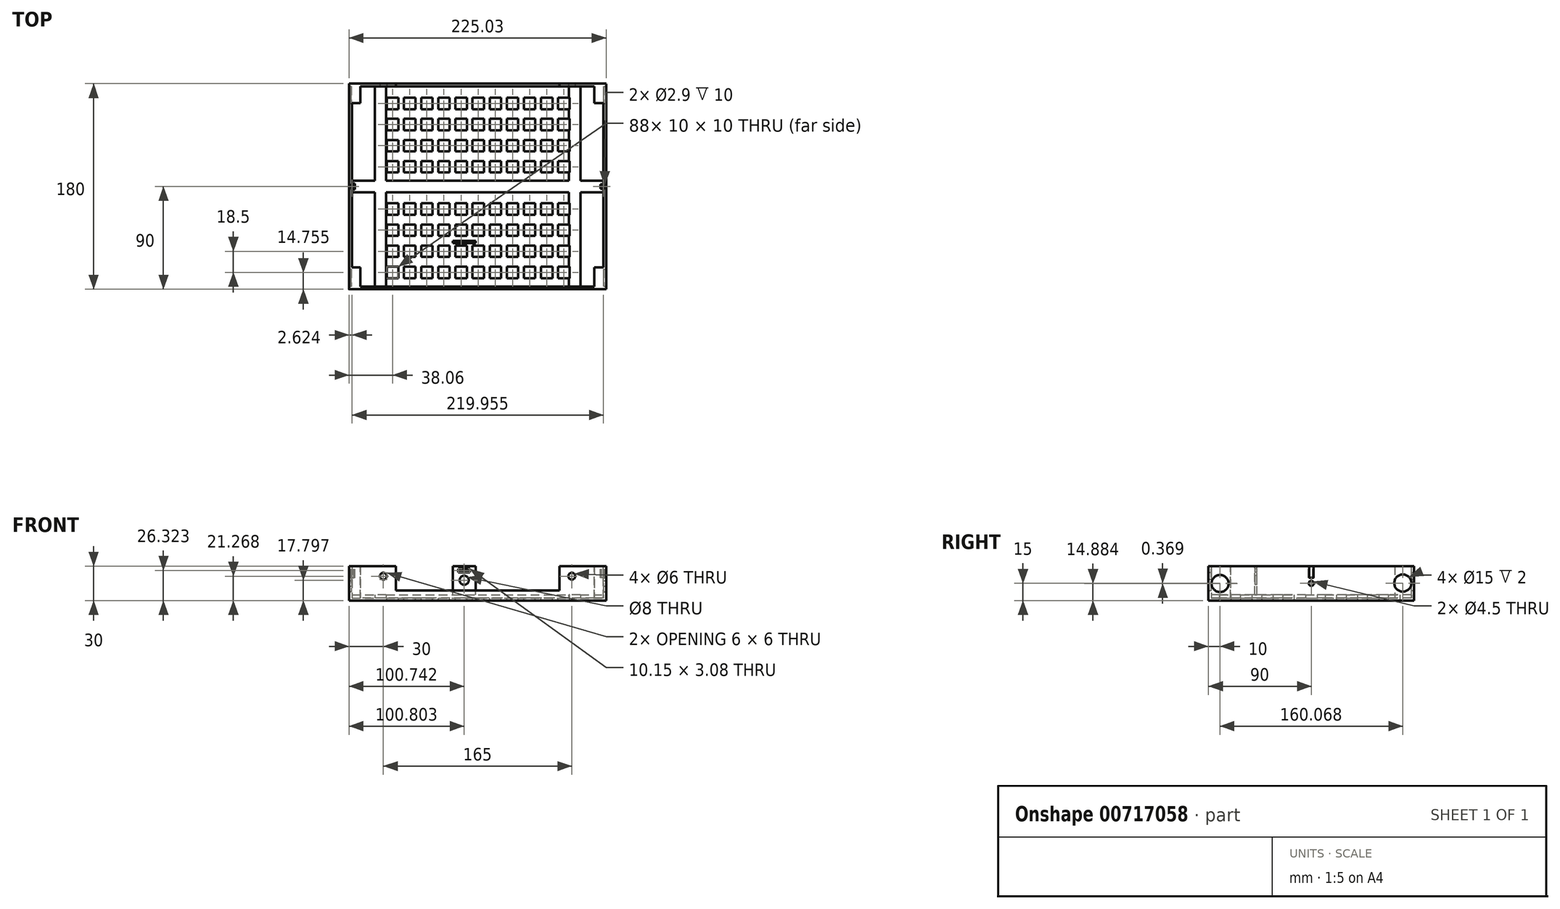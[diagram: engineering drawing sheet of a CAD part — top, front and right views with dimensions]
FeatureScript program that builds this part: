
annotation { "Feature Type Name" : "Feature", "Feature Type Description" : "" }
export const myFeature = defineFeature(function(context is Context, id is Id, definition is map)
    precondition{}
    {
        {
            var Q0;
            Q0=qCreatedBy(makeId("Top.planeOp"),FACE);
            var sketch = newSketch(context, id + "F0", { "sketchPlane" : qUnion([Q0])});
            skLineSegment(sketch, "E0.bottom", {"start": v(112.5, -90) * mm, "end": v(-112.5, -90) * mm});
            skLineSegment(sketch, "E0.top", {"start": v(112.5, 90) * mm, "end": v(-112.5, 90) * mm});
            skLineSegment(sketch, "E0.left", {"start": v(112.5, -90) * mm, "end": v(112.5, 90) * mm});
            skLineSegment(sketch, "E0.right", {"start": v(-112.5, -90) * mm, "end": v(-112.5, 90) * mm});
            skPoint(sketch, "E0.middle", {"position": v(0, 0) * mm});
            skSolve(sketch);
        }
        {
            var Q0;
            Q0=makeQuery(id+"F0.imprint","IMPRINT",FACE,{"disambiguationData":[TD([[makeQuery(id+"F0.imprint","IMPRINT",EDGE,{"derivedFrom":sQuery(id+"F0.wireOp",EDGE,"E0.bottom")}),-1.0]])]});
            extrude(context, id + "F1", {"entities" : qUnion([Q0]), "depth" : 30 * mm, "offsetDistance" : 25 * mm});
        }
        {
            var Q0;
            Q0=makeQuery(id+"F1.opExtrude","CAP_FACE",FACE,{"disambiguationData":[OSD([sQuery(id+"F0.wireOp",EDGE,"E0.bottom"),sQuery(id+"F0.wireOp",EDGE,"E0.top"),sQuery(id+"F0.wireOp",EDGE,"E0.left"),sQuery(id+"F0.wireOp",EDGE,"E0.right")])],"isStart":false});
            var sketch = newSketch(context, id + "F2", { "sketchPlane" : qUnion([Q0])});
            skLineSegment(sketch, "E1.bottom", {"start": v(110, -87.5) * mm, "end": v(-110, -87.5) * mm});
            skLineSegment(sketch, "E1.top", {"start": v(110, 87.5) * mm, "end": v(-110, 87.5) * mm});
            skLineSegment(sketch, "E1.left", {"start": v(110, -87.5) * mm, "end": v(110, 87.5) * mm});
            skLineSegment(sketch, "E1.right", {"start": v(-110, -87.5) * mm, "end": v(-110, 87.5) * mm});
            skPoint(sketch, "E1.middle", {"position": v(0, 0) * mm});
            skSolve(sketch);
        }
        {
            var Q0;
            Q0=makeQuery(id+"F2.imprint","IMPRINT",FACE,{"disambiguationData":[TD([[makeQuery(id+"F2.imprint","IMPRINT",EDGE,{"derivedFrom":sQuery(id+"F2.wireOp",EDGE,"E1.bottom")}),-1.0]])]});
            extrude(context, id + "F3", {"entities" : qUnion([Q0]), "operationType" : NewBodyOperationType.REMOVE, "oppositeDirection" : true, "depth" : 28 * mm, "offsetDistance" : 25 * mm});
        }
        {
            var Q0;
            Q0=makeQuery(id+"F1.opExtrude","SWEPT_FACE",FACE,{"disambiguationData":[OSD([sQuery(id+"F0.wireOp",EDGE,"E0.bottom")])]});
            var sketch = newSketch(context, id + "F4", { "sketchPlane" : qUnion([Q0])});
            skLineSegment(sketch, "E2", {"start": v(0, 15) * mm, "end": v(0, 30) * mm, "construction": true});
            skPoint(sketch, "E2.startSnap0", {"position": v(-112.5, 15) * mm});
            skPoint(sketch, "E2.startSnap1", {"position": v(0, 30) * mm});
            skLineSegment(sketch, "E3", {"start": v(0, 15) * mm, "end": v(-112.5, 15) * mm, "construction": true});
            skLineSegment(sketch, "E4", {"start": v(0, 15) * mm, "end": v(112.5, 15) * mm, "construction": true});
            skLineSegment(sketch, "E5", {"start": v(-112.5, 0) * mm, "end": v(-82.5, 0) * mm, "construction": true});
            skLineSegment(sketch, "E6", {"start": v(112.5, 0) * mm, "end": v(82.5, 0) * mm, "construction": true});
            skLineSegment(sketch, "E7", {"start": v(-82.5, 0) * mm, "end": v(-82.5, 30) * mm, "construction": true});
            skLineSegment(sketch, "E8", {"start": v(82.5, 0) * mm, "end": v(82.5, 30) * mm, "construction": true});
            skLineSegment(sketch, "E9", {"start": v(-112.5, 30) * mm, "end": v(-72.5, 30) * mm, "construction": true});
            skLineSegment(sketch, "E10", {"start": v(112.5, 30) * mm, "end": v(72.5, 30) * mm, "construction": true});
            skLineSegment(sketch, "E11", {"start": v(-112.5, 0) * mm, "end": v(-112.5, 10) * mm, "construction": true});
            skLineSegment(sketch, "E12", {"start": v(-112.5, 10) * mm, "end": v(112.5, 10) * mm, "construction": true});
            skLineSegment(sketch, "E13", {"start": v(-22.5, 30) * mm, "end": v(-22.5, 0) * mm, "construction": true});
            skLineSegment(sketch, "E14", {"start": v(22.5, 30) * mm, "end": v(22.5, 0) * mm, "construction": true});
            skFitSpline(sketch, "E15", {"points": [v(-72.5, 30) * mm, v(-71.2, 15) * mm, v(-22.5, 10) * mm], "startDerivative": vector(-3.64, -53.35) * mm, "endDerivative": vector(76.18, -37.14) * mm});
            skFitSpline(sketch, "E16", {"points": [v(72.5, 30) * mm, v(72.49, 15) * mm, v(22.5, 10) * mm], "startDerivative": vector(-2.42, -56.98) * mm, "endDerivative": vector(-66.73, -35.72) * mm});
            skLineSegment(sketch, "E17", {"start": v(-22.5, 10) * mm, "end": v(-22.5, 0) * mm});
            skLineSegment(sketch, "E18", {"start": v(22.5, 10) * mm, "end": v(22.5, 0) * mm});
            skLineSegment(sketch, "E19", {"start": v(-22.5, 10) * mm, "end": v(22.5, 10) * mm});
            skLineSegment(sketch, "E20", {"start": v(112.5, 21.27) * mm, "end": v(-112.5, 21.27) * mm, "construction": true});
            skCircle(sketch, "E21", {"center": v(82.5, 21.27) * mm, "radius": 3 * mm});
            skCircle(sketch, "E22", {"center": v(-82.5, 21.27) * mm, "radius": 3 * mm});
            skSolve(sketch);
        }
        {
            var Q0;
            Q0 = qSketchRegion(id + "F4", true);
            extrude(context, id + "F5", {"entities" : qUnion([Q0]), "operationType" : NewBodyOperationType.REMOVE, "oppositeDirection" : true, "depth" : 2500 * mm, "offsetDistance" : 25 * mm});
        }
        {
            var Q0;
            Q0=makeQuery(id+"F3.boolean.opBoolean","COPY",FACE,{"derivedFrom":makeQuery(id+"F3.opExtrude","CAP_FACE",FACE,{"disambiguationData":[OSD([sQuery(id+"F2.wireOp",EDGE,"E1.bottom"),sQuery(id+"F2.wireOp",EDGE,"E1.top"),sQuery(id+"F2.wireOp",EDGE,"E1.left"),sQuery(id+"F2.wireOp",EDGE,"E1.right")])],"isStart":false})});
            var sketch = newSketch(context, id + "F6", { "sketchPlane" : qUnion([Q0])});
            skLineSegment(sketch, "E23", {"start": v(-110, 87.5) * mm, "end": v(-90, 87.5) * mm, "construction": true});
            skLineSegment(sketch, "E24.bottom", {"start": v(-90, 87.5) * mm, "end": v(-80, 87.5) * mm});
            skLineSegment(sketch, "E24.top", {"start": v(-90, -87.5) * mm, "end": v(-80, -87.5) * mm});
            skLineSegment(sketch, "E24.left", {"start": v(-90, 87.5) * mm, "end": v(-90, -87.5) * mm});
            skLineSegment(sketch, "E24.right", {"start": v(-80, 87.5) * mm, "end": v(-80, -87.5) * mm});
            skLineSegment(sketch, "E25", {"start": v(110, 87.5) * mm, "end": v(90, 87.5) * mm, "construction": true});
            skLineSegment(sketch, "E26.bottom", {"start": v(90, 87.5) * mm, "end": v(80, 87.5) * mm});
            skLineSegment(sketch, "E26.top", {"start": v(90, -87.5) * mm, "end": v(80, -87.5) * mm});
            skLineSegment(sketch, "E26.left", {"start": v(90, 87.5) * mm, "end": v(90, -87.5) * mm});
            skLineSegment(sketch, "E26.right", {"start": v(80, 87.5) * mm, "end": v(80, -87.5) * mm});
            skLineSegment(sketch, "E27.bottom", {"start": v(-110, 5) * mm, "end": v(110, 5) * mm});
            skLineSegment(sketch, "E27.top", {"start": v(-110, -5) * mm, "end": v(110, -5) * mm});
            skLineSegment(sketch, "E27.left", {"start": v(-110, 5) * mm, "end": v(-110, -5) * mm});
            skLineSegment(sketch, "E27.right", {"start": v(110, 5) * mm, "end": v(110, -5) * mm});
            skPoint(sketch, "E27.middle", {"position": v(0, 0) * mm});
            skSolve(sketch);
        }
        {
            var Q0;
            Q0=makeQuery(id+"F6.imprint","IMPRINT",FACE,{"disambiguationData":[TD([[makeQuery(id+"F6.imprint","IMPRINT",EDGE,{"derivedFrom":sQuery(id+"F6.wireOp",EDGE,"E24.bottom")}),1.0]])]});
            var Q1;
            Q1=makeQuery(id+"F6.imprint","IMPRINT",FACE,{"disambiguationData":[TD([[makeQuery(id+"F6.imprint","IMPRINT",EDGE,{"derivedFrom":sQuery(id+"F6.wireOp",EDGE,"E26.bottom")}),1.0]])]});
            var Q2;
            {var subQ5=sQuery(id+"F6.wireOp",EDGE,"E27.left");Q2=makeQuery(id+"F6.imprint","IMPRINT",FACE,{"disambiguationData":[TD([[makeQuery(id+"F6.imprint","IMPRINT",EDGE,{"derivedFrom":subQ5}),-1.0]])]});}
            var Q3;
            {var subQ0=sQuery(id+"F6.wireOp",EDGE,"E27.bottom");var subQ1=sQuery(id+"F6.wireOp",EDGE,"E24.left");var subQ2=makeQuery(id+"F6.imprint","INTERSECT",VERTEX,{"derivedFrom":[subQ1,subQ0]});Q3=makeQuery(id+"F6.imprint","IMPRINT",FACE,{"disambiguationData":[TD([[makeQuery(id+"F6.imprint","IMPRINT",EDGE,{"disambiguationData":[TD([[subQ2,-1.0]])],"derivedFrom":subQ1}),1.0]])]});}
            var Q4;
            {var subQ0=sQuery(id+"F6.wireOp",EDGE,"E24.top");Q4=makeQuery(id+"F6.imprint","IMPRINT",FACE,{"disambiguationData":[TD([[makeQuery(id+"F6.imprint","IMPRINT",EDGE,{"derivedFrom":subQ0}),-1.0]])]});}
            var Q5;
            {var subQ0=sQuery(id+"F6.wireOp",EDGE,"E27.bottom");var subQ1=sQuery(id+"F6.wireOp",EDGE,"E24.right");var subQ2=makeQuery(id+"F6.imprint","INTERSECT",VERTEX,{"derivedFrom":[subQ1,subQ0]});Q5=makeQuery(id+"F6.imprint","IMPRINT",FACE,{"disambiguationData":[TD([[makeQuery(id+"F6.imprint","IMPRINT",EDGE,{"disambiguationData":[TD([[subQ2,-1.0]])],"derivedFrom":subQ1}),1.0]])]});}
            var Q6;
            {var subQ0=sQuery(id+"F6.wireOp",EDGE,"E27.bottom");var subQ1=sQuery(id+"F6.wireOp",EDGE,"E26.left");var subQ2=makeQuery(id+"F6.imprint","INTERSECT",VERTEX,{"derivedFrom":[subQ1,subQ0]});Q6=makeQuery(id+"F6.imprint","IMPRINT",FACE,{"disambiguationData":[TD([[makeQuery(id+"F6.imprint","IMPRINT",EDGE,{"disambiguationData":[TD([[subQ2,-1.0]])],"derivedFrom":subQ1}),-1.0]])]});}
            var Q7;
            {var subQ0=sQuery(id+"F6.wireOp",EDGE,"E26.top");Q7=makeQuery(id+"F6.imprint","IMPRINT",FACE,{"disambiguationData":[TD([[makeQuery(id+"F6.imprint","IMPRINT",EDGE,{"derivedFrom":subQ0}),-1.0]])]});}
            var Q8;
            {var subQ5=sQuery(id+"F6.wireOp",EDGE,"E27.right");Q8=makeQuery(id+"F6.imprint","IMPRINT",FACE,{"disambiguationData":[TD([[makeQuery(id+"F6.imprint","IMPRINT",EDGE,{"derivedFrom":subQ5}),1.0]])]});}
            extrude(context, id + "F7", {"entities" : qUnion([Q0, Q1, Q2, Q3, Q4, Q5, Q6, Q7, Q8]), "depth" : 3 * mm, "offsetDistance" : 25 * mm});
        }
        {
            var Q0;
            Q0=makeQuery(id+"F1.opExtrude","SWEPT_FACE",FACE,{"disambiguationData":[OSD([sQuery(id+"F0.wireOp",EDGE,"E0.left")])]});
            var sketch = newSketch(context, id + "F8", { "sketchPlane" : qUnion([Q0])});
            skLineSegment(sketch, "E28", {"start": v(0, 30) * mm, "end": v(0, 0) * mm, "construction": true});
            skLineSegment(sketch, "E29", {"start": v(-90, 15) * mm, "end": v(90, 15) * mm, "construction": true});
            skCircle(sketch, "E30", {"center": v(0, 15) * mm, "radius": 2.25 * mm});
            skSolve(sketch);
        }
        {
            var Q0;
            Q0=makeQuery(id+"F8.imprint","IMPRINT",FACE,{"disambiguationData":[TD([[makeQuery(id+"F8.imprint","IMPRINT",EDGE,{"derivedFrom":sQuery(id+"F8.wireOp",EDGE,"E30")}),1.0]])]});
            extrude(context, id + "F9", {"entities" : qUnion([Q0]), "operationType" : NewBodyOperationType.REMOVE, "endBound" : BoundingType.THROUGH_ALL, "oppositeDirection" : true, "depth" : 25 * mm, "offsetDistance" : 25 * mm});
        }
        {
            var Q0;
            Q0=makeQuery(id+"F1.opExtrude","SWEPT_FACE",FACE,{"disambiguationData":[OSD([sQuery(id+"F0.wireOp",EDGE,"E0.top")])]});
            var sketch = newSketch(context, id + "F10", { "sketchPlane" : qUnion([Q0])});
            skLineSegment(sketch, "E31.bottom", {"start": v(71.59, 8.69) * mm, "end": v(-71.59, 8.69) * mm});
            skLineSegment(sketch, "E31.top", {"start": v(71.59, 51.31) * mm, "end": v(-71.59, 51.31) * mm});
            skLineSegment(sketch, "E31.left", {"start": v(71.59, 8.69) * mm, "end": v(71.59, 51.31) * mm});
            skLineSegment(sketch, "E31.right", {"start": v(-71.59, 8.69) * mm, "end": v(-71.59, 51.31) * mm});
            skPoint(sketch, "E31.middle", {"position": v(0, 30) * mm});
            skSolve(sketch);
        }
        {
            var Q0;
            {var subQ0=sQuery(id+"F10.wireOp",EDGE,"E31.bottom");Q0=makeQuery(id+"F10.imprint","IMPRINT",FACE,{"disambiguationData":[TD([[makeQuery(id+"F10.imprint","IMPRINT",EDGE,{"derivedFrom":subQ0}),-1.0]])]});}
            extrude(context, id + "F11", {"entities" : qUnion([Q0]), "operationType" : NewBodyOperationType.REMOVE, "oppositeDirection" : true, "depth" : 3000 * mm, "offsetDistance" : 25 * mm});
        }
        {
            var Q0;
            Q0=makeQuery(id+"F2.imprint","IMPRINT",FACE,{"disambiguationData":[TD([[makeQuery(id+"F2.imprint","IMPRINT",EDGE,{"derivedFrom":sQuery(id+"F2.wireOp",EDGE,"E1.bottom")}),-1.0]])]});
            var sketch = newSketch(context, id + "F12", { "sketchPlane" : qUnion([Q0])});
            skLineSegment(sketch, "E32.bottom", {"start": v(-112.4, 89.96) * mm, "end": v(-102.7, 89.96) * mm});
            skLineSegment(sketch, "E32.top", {"start": v(-112.4, 72.97) * mm, "end": v(-102.7, 72.97) * mm});
            skLineSegment(sketch, "E32.left", {"start": v(-112.4, 89.96) * mm, "end": v(-112.4, 72.97) * mm});
            skLineSegment(sketch, "E32.right", {"start": v(-102.7, 89.96) * mm, "end": v(-102.7, 72.97) * mm});
            skLineSegment(sketch, "E33.bottom", {"start": v(-112.5, -89.96) * mm, "end": v(-102.68, -89.96) * mm});
            skLineSegment(sketch, "E33.top", {"start": v(-112.5, -70.82) * mm, "end": v(-102.68, -70.82) * mm});
            skLineSegment(sketch, "E33.left", {"start": v(-112.5, -89.96) * mm, "end": v(-112.5, -70.82) * mm});
            skLineSegment(sketch, "E33.right", {"start": v(-102.68, -89.96) * mm, "end": v(-102.68, -70.82) * mm});
            skLineSegment(sketch, "E34.bottom", {"start": v(112.5, 89.98) * mm, "end": v(102.19, 89.98) * mm});
            skLineSegment(sketch, "E34.top", {"start": v(112.5, 72.97) * mm, "end": v(102.19, 72.97) * mm});
            skLineSegment(sketch, "E34.left", {"start": v(112.5, 89.98) * mm, "end": v(112.5, 72.97) * mm});
            skLineSegment(sketch, "E34.right", {"start": v(102.19, 89.98) * mm, "end": v(102.19, 72.97) * mm});
            skLineSegment(sketch, "E35.bottom", {"start": v(112.45, -89.96) * mm, "end": v(102.2, -89.96) * mm});
            skLineSegment(sketch, "E35.top", {"start": v(112.45, -70.67) * mm, "end": v(102.2, -70.67) * mm});
            skLineSegment(sketch, "E35.left", {"start": v(112.45, -89.96) * mm, "end": v(112.45, -70.67) * mm});
            skLineSegment(sketch, "E35.right", {"start": v(102.2, -89.96) * mm, "end": v(102.2, -70.67) * mm});
            skLineSegment(sketch, "E36", {"start": v(-102.7, -93.75) * mm, "end": v(-102.7, 94.08) * mm, "construction": true});
            skLineSegment(sketch, "E37", {"start": v(-116.28, -70.82) * mm, "end": v(124.38, -70.82) * mm, "construction": true});
            skLineSegment(sketch, "E38", {"start": v(-119.93, 72.97) * mm, "end": v(152.22, 72.97) * mm, "construction": true});
            skLineSegment(sketch, "E39", {"start": v(102.19, 97.41) * mm, "end": v(102.19, -106.67) * mm, "construction": true});
            skSolve(sketch);
        }
        {
            var Q0;
            Q0 = qSketchRegion(id + "F12", true);
            extrude(context, id + "F13", {"entities" : qUnion([Q0]), "operationType" : NewBodyOperationType.ADD, "oppositeDirection" : true, "depth" : 30 * mm, "offsetDistance" : 25 * mm});
        }
        {
            var Q0;
            Q0=makeQuery(id+"F1.opExtrude","SWEPT_FACE",FACE,{"disambiguationData":[OSD([sQuery(id+"F0.wireOp",EDGE,"E0.right")])]});
            var sketch = newSketch(context, id + "F14", { "sketchPlane" : qUnion([Q0])});
            skLineSegment(sketch, "E40", {"start": v(-80, 30) * mm, "end": v(-80, 0) * mm, "construction": true});
            skLineSegment(sketch, "E41", {"start": v(80, 30) * mm, "end": v(80, 0) * mm, "construction": true});
            skCircle(sketch, "E42", {"center": v(-80, 15) * mm, "radius": 7.5 * mm});
            skCircle(sketch, "E43", {"center": v(80, 15) * mm, "radius": 7.5 * mm});
            skSolve(sketch);
        }
        {
            var Q0;
            Q0 = qSketchRegion(id + "F14", true);
            extrude(context, id + "F15", {"entities" : qUnion([Q0]), "operationType" : NewBodyOperationType.REMOVE, "oppositeDirection" : true, "depth" : 2 * mm, "offsetDistance" : 25 * mm});
        }
        {
            var Q0;
            Q0=makeQuery(id+"F8.imprint","IMPRINT",FACE,{"disambiguationData":[TD([[makeQuery(id+"F8.imprint","IMPRINT",EDGE,{"derivedFrom":sQuery(id+"F8.wireOp",EDGE,"E30")}),-1.0]])]});
            var sketch = newSketch(context, id + "F16", { "sketchPlane" : qUnion([Q0])});
            skCircle(sketch, "E44", {"center": v(-79.9, 14.88) * mm, "radius": 7.5 * mm});
            skCircle(sketch, "E45", {"center": v(80.07, 15.25) * mm, "radius": 7.5 * mm});
            skSolve(sketch);
        }
        {
            var Q0;
            Q0 = qSketchRegion(id + "F16", true);
            extrude(context, id + "F17", {"entities" : qUnion([Q0]), "operationType" : NewBodyOperationType.REMOVE, "oppositeDirection" : true, "depth" : 2 * mm, "offsetDistance" : 25 * mm});
        }
        {
            var Q0;
            {var subQ0=sQuery(id+"F12.wireOp",EDGE,"E32.right");var subQ17=sQuery(id+"F12.wireOp",EDGE,"E32.top");var subQ18=makeQuery(id+"F12.imprint","INTERSECT",VERTEX,{"derivedFrom":[subQ17,subQ0]});Q0=makeQuery(id+"F12.imprint","IMPRINT",FACE,{"disambiguationData":[TD([[makeQuery(id+"F12.imprint","IMPRINT",EDGE,{"disambiguationData":[TD([[subQ18,1.0]])],"derivedFrom":subQ17}),-1.0]])]});}
            var sketch = newSketch(context, id + "F18", { "sketchPlane" : qUnion([Q0])});
            skLineSegment(sketch, "E46", {"start": v(-21.73, -47.51) * mm, "end": v(-1.73, -47.51) * mm});
            skLineSegment(sketch, "E47", {"start": v(-1.73, -47.51) * mm, "end": v(-1.73, -49.51) * mm});
            skLineSegment(sketch, "E48", {"start": v(-1.73, -49.51) * mm, "end": v(-21.73, -49.51) * mm});
            skLineSegment(sketch, "E49", {"start": v(-21.73, -49.51) * mm, "end": v(-21.73, -47.51) * mm});
            skSolve(sketch);
        }
        {
            var Q0;
            Q0=makeQuery(id+"F18.imprint","IMPRINT",FACE,{"disambiguationData":[TD([[makeQuery(id+"F18.imprint","IMPRINT",EDGE,{"derivedFrom":sQuery(id+"F18.wireOp",EDGE,"E46")}),-1.0]])]});
            extrude(context, id + "F19", {"entities" : qUnion([Q0]), "operationType" : NewBodyOperationType.ADD, "oppositeDirection" : true, "depth" : 25 * mm, "offsetDistance" : 25 * mm});
        }
        {
            var Q0;
            {var subQ0=sQuery(id+"F4.wireOp",EDGE,"E15");Q0=makeQuery(id+"F4.imprint","IMPRINT",FACE,{"disambiguationData":[TD([[makeQuery(id+"F4.imprint","IMPRINT",EDGE,{"derivedFrom":subQ0}),1.0]])]});}
            var sketch = newSketch(context, id + "F20", { "sketchPlane" : qUnion([Q0])});
            skCircle(sketch, "E50", {"center": v(-11.7, 17.8) * mm, "radius": 4 * mm});
            skSolve(sketch);
        }
        {
            var Q0;
            Q0 = qSketchRegion(id + "F20", true);
            extrude(context, id + "F21", {"entities" : qUnion([Q0]), "operationType" : NewBodyOperationType.REMOVE, "oppositeDirection" : true, "depth" : 3000 * mm, "offsetDistance" : 25 * mm});
        }
        {
            var Q0;
            {var subQ4=sQuery(id+"F4.wireOp",EDGE,"E15");Q0=makeQuery(id+"F4.imprint","IMPRINT",FACE,{"disambiguationData":[TD([[makeQuery(id+"F4.imprint","IMPRINT",EDGE,{"derivedFrom":subQ4}),-1.0]])]});}
            var sketch = newSketch(context, id + "F22", { "sketchPlane" : qUnion([Q0])});
            skLineSegment(sketch, "E51.bottom", {"start": v(-6.68, 24.78) * mm, "end": v(-16.83, 24.78) * mm});
            skLineSegment(sketch, "E51.top", {"start": v(-6.68, 27.86) * mm, "end": v(-16.83, 27.86) * mm});
            skLineSegment(sketch, "E51.left", {"start": v(-6.68, 24.78) * mm, "end": v(-6.68, 27.86) * mm});
            skLineSegment(sketch, "E51.right", {"start": v(-16.83, 24.78) * mm, "end": v(-16.83, 27.86) * mm});
            skPoint(sketch, "E51.middle", {"position": v(-11.76, 26.32) * mm});
            skSolve(sketch);
        }
        {
            var Q0;
            Q0 = qSketchRegion(id + "F22", true);
            extrude(context, id + "F23", {"entities" : qUnion([Q0]), "operationType" : NewBodyOperationType.REMOVE, "oppositeDirection" : true, "depth" : 3000 * mm, "offsetDistance" : 25 * mm});
        }
        {
            var Q0;
            Q0=makeQuery(id+"F0.imprint","IMPRINT",FACE,{"disambiguationData":[TD([[makeQuery(id+"F0.imprint","IMPRINT",EDGE,{"derivedFrom":sQuery(id+"F0.wireOp",EDGE,"E0.bottom")}),-1.0]])]});
            var sketch = newSketch(context, id + "F24", { "sketchPlane" : qUnion([Q0])});
            skLineSegment(sketch, "E52.bottom", {"start": v(-69.44, -80.25) * mm, "end": v(-79.44, -80.25) * mm});
            skLineSegment(sketch, "E52.top", {"start": v(-69.44, -70.25) * mm, "end": v(-79.44, -70.25) * mm});
            skLineSegment(sketch, "E52.left", {"start": v(-69.44, -80.25) * mm, "end": v(-69.44, -70.25) * mm});
            skLineSegment(sketch, "E52.right", {"start": v(-79.44, -80.25) * mm, "end": v(-79.44, -70.25) * mm});
            skPoint(sketch, "E52.middle", {"position": v(-74.44, -75.25) * mm});
            skPoint(sketch, "E53.0.1.0", {"position": v(-74.44, -56.75) * mm});
            skLineSegment(sketch, "E53.0.1.1", {"start": v(-69.44, -61.75) * mm, "end": v(-69.44, -51.75) * mm});
            skLineSegment(sketch, "E53.0.1.2", {"start": v(-69.44, -51.75) * mm, "end": v(-79.44, -51.75) * mm});
            skLineSegment(sketch, "E53.0.1.3", {"start": v(-69.44, -61.75) * mm, "end": v(-79.44, -61.75) * mm});
            skLineSegment(sketch, "E53.0.1.4", {"start": v(-79.44, -61.75) * mm, "end": v(-79.44, -51.75) * mm});
            skPoint(sketch, "E53.0.2.0", {"position": v(-74.44, -38.25) * mm});
            skLineSegment(sketch, "E53.0.2.1", {"start": v(-69.44, -43.25) * mm, "end": v(-69.44, -33.25) * mm});
            skLineSegment(sketch, "E53.0.2.2", {"start": v(-69.44, -33.25) * mm, "end": v(-79.44, -33.25) * mm});
            skLineSegment(sketch, "E53.0.2.3", {"start": v(-69.44, -43.25) * mm, "end": v(-79.44, -43.25) * mm});
            skLineSegment(sketch, "E53.0.2.4", {"start": v(-79.44, -43.25) * mm, "end": v(-79.44, -33.25) * mm});
            skPoint(sketch, "E53.0.3.0", {"position": v(-74.44, -19.75) * mm});
            skLineSegment(sketch, "E53.0.3.1", {"start": v(-69.44, -24.75) * mm, "end": v(-69.44, -14.75) * mm});
            skLineSegment(sketch, "E53.0.3.2", {"start": v(-69.44, -14.75) * mm, "end": v(-79.44, -14.75) * mm});
            skLineSegment(sketch, "E53.0.3.3", {"start": v(-69.44, -24.75) * mm, "end": v(-79.44, -24.75) * mm});
            skLineSegment(sketch, "E53.0.3.4", {"start": v(-79.44, -24.75) * mm, "end": v(-79.44, -14.75) * mm});
            skPoint(sketch, "E53.0.5.0", {"position": v(-74.44, 17.25) * mm});
            skLineSegment(sketch, "E53.0.5.1", {"start": v(-69.44, 12.25) * mm, "end": v(-69.44, 22.25) * mm});
            skLineSegment(sketch, "E53.0.5.2", {"start": v(-69.44, 22.25) * mm, "end": v(-79.44, 22.25) * mm});
            skLineSegment(sketch, "E53.0.5.3", {"start": v(-69.44, 12.25) * mm, "end": v(-79.44, 12.25) * mm});
            skLineSegment(sketch, "E53.0.5.4", {"start": v(-79.44, 12.25) * mm, "end": v(-79.44, 22.25) * mm});
            skPoint(sketch, "E53.0.6.0", {"position": v(-74.44, 35.75) * mm});
            skLineSegment(sketch, "E53.0.6.1", {"start": v(-69.44, 30.75) * mm, "end": v(-69.44, 40.75) * mm});
            skLineSegment(sketch, "E53.0.6.2", {"start": v(-69.44, 40.75) * mm, "end": v(-79.44, 40.75) * mm});
            skLineSegment(sketch, "E53.0.6.3", {"start": v(-69.44, 30.75) * mm, "end": v(-79.44, 30.75) * mm});
            skLineSegment(sketch, "E53.0.6.4", {"start": v(-79.44, 30.75) * mm, "end": v(-79.44, 40.75) * mm});
            skPoint(sketch, "E53.0.7.0", {"position": v(-74.44, 54.25) * mm});
            skLineSegment(sketch, "E53.0.7.1", {"start": v(-69.44, 49.25) * mm, "end": v(-69.44, 59.25) * mm});
            skLineSegment(sketch, "E53.0.7.2", {"start": v(-69.44, 59.25) * mm, "end": v(-79.44, 59.25) * mm});
            skLineSegment(sketch, "E53.0.7.3", {"start": v(-69.44, 49.25) * mm, "end": v(-79.44, 49.25) * mm});
            skLineSegment(sketch, "E53.0.7.4", {"start": v(-79.44, 49.25) * mm, "end": v(-79.44, 59.25) * mm});
            skPoint(sketch, "E53.0.8.0", {"position": v(-74.44, 72.75) * mm});
            skLineSegment(sketch, "E53.0.8.1", {"start": v(-69.44, 67.75) * mm, "end": v(-69.44, 77.75) * mm});
            skLineSegment(sketch, "E53.0.8.2", {"start": v(-69.44, 77.75) * mm, "end": v(-79.44, 77.75) * mm});
            skLineSegment(sketch, "E53.0.8.3", {"start": v(-69.44, 67.75) * mm, "end": v(-79.44, 67.75) * mm});
            skLineSegment(sketch, "E53.0.8.4", {"start": v(-79.44, 67.75) * mm, "end": v(-79.44, 77.75) * mm});
            skPoint(sketch, "E53.1.0.0", {"position": v(-59.44, -75.25) * mm});
            skLineSegment(sketch, "E53.1.0.1", {"start": v(-54.44, -80.25) * mm, "end": v(-54.44, -70.25) * mm});
            skLineSegment(sketch, "E53.1.0.2", {"start": v(-54.44, -70.25) * mm, "end": v(-64.44, -70.25) * mm});
            skLineSegment(sketch, "E53.1.0.3", {"start": v(-54.44, -80.25) * mm, "end": v(-64.44, -80.25) * mm});
            skLineSegment(sketch, "E53.1.0.4", {"start": v(-64.44, -80.25) * mm, "end": v(-64.44, -70.25) * mm});
            skPoint(sketch, "E53.1.1.0", {"position": v(-59.44, -56.75) * mm});
            skLineSegment(sketch, "E53.1.1.1", {"start": v(-54.44, -61.75) * mm, "end": v(-54.44, -51.75) * mm});
            skLineSegment(sketch, "E53.1.1.2", {"start": v(-54.44, -51.75) * mm, "end": v(-64.44, -51.75) * mm});
            skLineSegment(sketch, "E53.1.1.3", {"start": v(-54.44, -61.75) * mm, "end": v(-64.44, -61.75) * mm});
            skLineSegment(sketch, "E53.1.1.4", {"start": v(-64.44, -61.75) * mm, "end": v(-64.44, -51.75) * mm});
            skPoint(sketch, "E53.1.2.0", {"position": v(-59.44, -38.25) * mm});
            skLineSegment(sketch, "E53.1.2.1", {"start": v(-54.44, -43.25) * mm, "end": v(-54.44, -33.25) * mm});
            skLineSegment(sketch, "E53.1.2.2", {"start": v(-54.44, -33.25) * mm, "end": v(-64.44, -33.25) * mm});
            skLineSegment(sketch, "E53.1.2.3", {"start": v(-54.44, -43.25) * mm, "end": v(-64.44, -43.25) * mm});
            skLineSegment(sketch, "E53.1.2.4", {"start": v(-64.44, -43.25) * mm, "end": v(-64.44, -33.25) * mm});
            skPoint(sketch, "E53.1.3.0", {"position": v(-59.44, -19.75) * mm});
            skLineSegment(sketch, "E53.1.3.1", {"start": v(-54.44, -24.75) * mm, "end": v(-54.44, -14.75) * mm});
            skLineSegment(sketch, "E53.1.3.2", {"start": v(-54.44, -14.75) * mm, "end": v(-64.44, -14.75) * mm});
            skLineSegment(sketch, "E53.1.3.3", {"start": v(-54.44, -24.75) * mm, "end": v(-64.44, -24.75) * mm});
            skLineSegment(sketch, "E53.1.3.4", {"start": v(-64.44, -24.75) * mm, "end": v(-64.44, -14.75) * mm});
            skPoint(sketch, "E53.1.5.0", {"position": v(-59.44, 17.25) * mm});
            skLineSegment(sketch, "E53.1.5.1", {"start": v(-54.44, 12.25) * mm, "end": v(-54.44, 22.25) * mm});
            skLineSegment(sketch, "E53.1.5.2", {"start": v(-54.44, 22.25) * mm, "end": v(-64.44, 22.25) * mm});
            skLineSegment(sketch, "E53.1.5.3", {"start": v(-54.44, 12.25) * mm, "end": v(-64.44, 12.25) * mm});
            skLineSegment(sketch, "E53.1.5.4", {"start": v(-64.44, 12.25) * mm, "end": v(-64.44, 22.25) * mm});
            skPoint(sketch, "E53.1.6.0", {"position": v(-59.44, 35.75) * mm});
            skLineSegment(sketch, "E53.1.6.1", {"start": v(-54.44, 30.75) * mm, "end": v(-54.44, 40.75) * mm});
            skLineSegment(sketch, "E53.1.6.2", {"start": v(-54.44, 40.75) * mm, "end": v(-64.44, 40.75) * mm});
            skLineSegment(sketch, "E53.1.6.3", {"start": v(-54.44, 30.75) * mm, "end": v(-64.44, 30.75) * mm});
            skLineSegment(sketch, "E53.1.6.4", {"start": v(-64.44, 30.75) * mm, "end": v(-64.44, 40.75) * mm});
            skPoint(sketch, "E53.1.7.0", {"position": v(-59.44, 54.25) * mm});
            skLineSegment(sketch, "E53.1.7.1", {"start": v(-54.44, 49.25) * mm, "end": v(-54.44, 59.25) * mm});
            skLineSegment(sketch, "E53.1.7.2", {"start": v(-54.44, 59.25) * mm, "end": v(-64.44, 59.25) * mm});
            skLineSegment(sketch, "E53.1.7.3", {"start": v(-54.44, 49.25) * mm, "end": v(-64.44, 49.25) * mm});
            skLineSegment(sketch, "E53.1.7.4", {"start": v(-64.44, 49.25) * mm, "end": v(-64.44, 59.25) * mm});
            skPoint(sketch, "E53.1.8.0", {"position": v(-59.44, 72.75) * mm});
            skLineSegment(sketch, "E53.1.8.1", {"start": v(-54.44, 67.75) * mm, "end": v(-54.44, 77.75) * mm});
            skLineSegment(sketch, "E53.1.8.2", {"start": v(-54.44, 77.75) * mm, "end": v(-64.44, 77.75) * mm});
            skLineSegment(sketch, "E53.1.8.3", {"start": v(-54.44, 67.75) * mm, "end": v(-64.44, 67.75) * mm});
            skLineSegment(sketch, "E53.1.8.4", {"start": v(-64.44, 67.75) * mm, "end": v(-64.44, 77.75) * mm});
            skPoint(sketch, "E53.2.0.0", {"position": v(-44.44, -75.25) * mm});
            skLineSegment(sketch, "E53.2.0.1", {"start": v(-39.44, -80.25) * mm, "end": v(-39.44, -70.25) * mm});
            skLineSegment(sketch, "E53.2.0.2", {"start": v(-39.44, -70.25) * mm, "end": v(-49.44, -70.25) * mm});
            skLineSegment(sketch, "E53.2.0.3", {"start": v(-39.44, -80.25) * mm, "end": v(-49.44, -80.25) * mm});
            skLineSegment(sketch, "E53.2.0.4", {"start": v(-49.44, -80.25) * mm, "end": v(-49.44, -70.25) * mm});
            skPoint(sketch, "E53.2.1.0", {"position": v(-44.44, -56.75) * mm});
            skLineSegment(sketch, "E53.2.1.1", {"start": v(-39.44, -61.75) * mm, "end": v(-39.44, -51.75) * mm});
            skLineSegment(sketch, "E53.2.1.2", {"start": v(-39.44, -51.75) * mm, "end": v(-49.44, -51.75) * mm});
            skLineSegment(sketch, "E53.2.1.3", {"start": v(-39.44, -61.75) * mm, "end": v(-49.44, -61.75) * mm});
            skLineSegment(sketch, "E53.2.1.4", {"start": v(-49.44, -61.75) * mm, "end": v(-49.44, -51.75) * mm});
            skPoint(sketch, "E53.2.2.0", {"position": v(-44.44, -38.25) * mm});
            skLineSegment(sketch, "E53.2.2.1", {"start": v(-39.44, -43.25) * mm, "end": v(-39.44, -33.25) * mm});
            skLineSegment(sketch, "E53.2.2.2", {"start": v(-39.44, -33.25) * mm, "end": v(-49.44, -33.25) * mm});
            skLineSegment(sketch, "E53.2.2.3", {"start": v(-39.44, -43.25) * mm, "end": v(-49.44, -43.25) * mm});
            skLineSegment(sketch, "E53.2.2.4", {"start": v(-49.44, -43.25) * mm, "end": v(-49.44, -33.25) * mm});
            skPoint(sketch, "E53.2.3.0", {"position": v(-44.44, -19.75) * mm});
            skLineSegment(sketch, "E53.2.3.1", {"start": v(-39.44, -24.75) * mm, "end": v(-39.44, -14.75) * mm});
            skLineSegment(sketch, "E53.2.3.2", {"start": v(-39.44, -14.75) * mm, "end": v(-49.44, -14.75) * mm});
            skLineSegment(sketch, "E53.2.3.3", {"start": v(-39.44, -24.75) * mm, "end": v(-49.44, -24.75) * mm});
            skLineSegment(sketch, "E53.2.3.4", {"start": v(-49.44, -24.75) * mm, "end": v(-49.44, -14.75) * mm});
            skPoint(sketch, "E53.2.5.0", {"position": v(-44.44, 17.25) * mm});
            skLineSegment(sketch, "E53.2.5.1", {"start": v(-39.44, 12.25) * mm, "end": v(-39.44, 22.25) * mm});
            skLineSegment(sketch, "E53.2.5.2", {"start": v(-39.44, 22.25) * mm, "end": v(-49.44, 22.25) * mm});
            skLineSegment(sketch, "E53.2.5.3", {"start": v(-39.44, 12.25) * mm, "end": v(-49.44, 12.25) * mm});
            skLineSegment(sketch, "E53.2.5.4", {"start": v(-49.44, 12.25) * mm, "end": v(-49.44, 22.25) * mm});
            skPoint(sketch, "E53.2.6.0", {"position": v(-44.44, 35.75) * mm});
            skLineSegment(sketch, "E53.2.6.1", {"start": v(-39.44, 30.75) * mm, "end": v(-39.44, 40.75) * mm});
            skLineSegment(sketch, "E53.2.6.2", {"start": v(-39.44, 40.75) * mm, "end": v(-49.44, 40.75) * mm});
            skLineSegment(sketch, "E53.2.6.3", {"start": v(-39.44, 30.75) * mm, "end": v(-49.44, 30.75) * mm});
            skLineSegment(sketch, "E53.2.6.4", {"start": v(-49.44, 30.75) * mm, "end": v(-49.44, 40.75) * mm});
            skPoint(sketch, "E53.2.7.0", {"position": v(-44.44, 54.25) * mm});
            skLineSegment(sketch, "E53.2.7.1", {"start": v(-39.44, 49.25) * mm, "end": v(-39.44, 59.25) * mm});
            skLineSegment(sketch, "E53.2.7.2", {"start": v(-39.44, 59.25) * mm, "end": v(-49.44, 59.25) * mm});
            skLineSegment(sketch, "E53.2.7.3", {"start": v(-39.44, 49.25) * mm, "end": v(-49.44, 49.25) * mm});
            skLineSegment(sketch, "E53.2.7.4", {"start": v(-49.44, 49.25) * mm, "end": v(-49.44, 59.25) * mm});
            skPoint(sketch, "E53.2.8.0", {"position": v(-44.44, 72.75) * mm});
            skLineSegment(sketch, "E53.2.8.1", {"start": v(-39.44, 67.75) * mm, "end": v(-39.44, 77.75) * mm});
            skLineSegment(sketch, "E53.2.8.2", {"start": v(-39.44, 77.75) * mm, "end": v(-49.44, 77.75) * mm});
            skLineSegment(sketch, "E53.2.8.3", {"start": v(-39.44, 67.75) * mm, "end": v(-49.44, 67.75) * mm});
            skLineSegment(sketch, "E53.2.8.4", {"start": v(-49.44, 67.75) * mm, "end": v(-49.44, 77.75) * mm});
            skPoint(sketch, "E53.3.0.0", {"position": v(-29.44, -75.25) * mm});
            skLineSegment(sketch, "E53.3.0.1", {"start": v(-24.44, -80.25) * mm, "end": v(-24.44, -70.25) * mm});
            skLineSegment(sketch, "E53.3.0.2", {"start": v(-24.44, -70.25) * mm, "end": v(-34.44, -70.25) * mm});
            skLineSegment(sketch, "E53.3.0.3", {"start": v(-24.44, -80.25) * mm, "end": v(-34.44, -80.25) * mm});
            skLineSegment(sketch, "E53.3.0.4", {"start": v(-34.44, -80.25) * mm, "end": v(-34.44, -70.25) * mm});
            skPoint(sketch, "E53.3.1.0", {"position": v(-29.44, -56.75) * mm});
            skLineSegment(sketch, "E53.3.1.1", {"start": v(-24.44, -61.75) * mm, "end": v(-24.44, -51.75) * mm});
            skLineSegment(sketch, "E53.3.1.2", {"start": v(-24.44, -51.75) * mm, "end": v(-34.44, -51.75) * mm});
            skLineSegment(sketch, "E53.3.1.3", {"start": v(-24.44, -61.75) * mm, "end": v(-34.44, -61.75) * mm});
            skLineSegment(sketch, "E53.3.1.4", {"start": v(-34.44, -61.75) * mm, "end": v(-34.44, -51.75) * mm});
            skPoint(sketch, "E53.3.2.0", {"position": v(-29.44, -38.25) * mm});
            skLineSegment(sketch, "E53.3.2.1", {"start": v(-24.44, -43.25) * mm, "end": v(-24.44, -33.25) * mm});
            skLineSegment(sketch, "E53.3.2.2", {"start": v(-24.44, -33.25) * mm, "end": v(-34.44, -33.25) * mm});
            skLineSegment(sketch, "E53.3.2.3", {"start": v(-24.44, -43.25) * mm, "end": v(-34.44, -43.25) * mm});
            skLineSegment(sketch, "E53.3.2.4", {"start": v(-34.44, -43.25) * mm, "end": v(-34.44, -33.25) * mm});
            skPoint(sketch, "E53.3.3.0", {"position": v(-29.44, -19.75) * mm});
            skLineSegment(sketch, "E53.3.3.1", {"start": v(-24.44, -24.75) * mm, "end": v(-24.44, -14.75) * mm});
            skLineSegment(sketch, "E53.3.3.2", {"start": v(-24.44, -14.75) * mm, "end": v(-34.44, -14.75) * mm});
            skLineSegment(sketch, "E53.3.3.3", {"start": v(-24.44, -24.75) * mm, "end": v(-34.44, -24.75) * mm});
            skLineSegment(sketch, "E53.3.3.4", {"start": v(-34.44, -24.75) * mm, "end": v(-34.44, -14.75) * mm});
            skPoint(sketch, "E53.3.5.0", {"position": v(-29.44, 17.25) * mm});
            skLineSegment(sketch, "E53.3.5.1", {"start": v(-24.44, 12.25) * mm, "end": v(-24.44, 22.25) * mm});
            skLineSegment(sketch, "E53.3.5.2", {"start": v(-24.44, 22.25) * mm, "end": v(-34.44, 22.25) * mm});
            skLineSegment(sketch, "E53.3.5.3", {"start": v(-24.44, 12.25) * mm, "end": v(-34.44, 12.25) * mm});
            skLineSegment(sketch, "E53.3.5.4", {"start": v(-34.44, 12.25) * mm, "end": v(-34.44, 22.25) * mm});
            skPoint(sketch, "E53.3.6.0", {"position": v(-29.44, 35.75) * mm});
            skLineSegment(sketch, "E53.3.6.1", {"start": v(-24.44, 30.75) * mm, "end": v(-24.44, 40.75) * mm});
            skLineSegment(sketch, "E53.3.6.2", {"start": v(-24.44, 40.75) * mm, "end": v(-34.44, 40.75) * mm});
            skLineSegment(sketch, "E53.3.6.3", {"start": v(-24.44, 30.75) * mm, "end": v(-34.44, 30.75) * mm});
            skLineSegment(sketch, "E53.3.6.4", {"start": v(-34.44, 30.75) * mm, "end": v(-34.44, 40.75) * mm});
            skPoint(sketch, "E53.3.7.0", {"position": v(-29.44, 54.25) * mm});
            skLineSegment(sketch, "E53.3.7.1", {"start": v(-24.44, 49.25) * mm, "end": v(-24.44, 59.25) * mm});
            skLineSegment(sketch, "E53.3.7.2", {"start": v(-24.44, 59.25) * mm, "end": v(-34.44, 59.25) * mm});
            skLineSegment(sketch, "E53.3.7.3", {"start": v(-24.44, 49.25) * mm, "end": v(-34.44, 49.25) * mm});
            skLineSegment(sketch, "E53.3.7.4", {"start": v(-34.44, 49.25) * mm, "end": v(-34.44, 59.25) * mm});
            skPoint(sketch, "E53.3.8.0", {"position": v(-29.44, 72.75) * mm});
            skLineSegment(sketch, "E53.3.8.1", {"start": v(-24.44, 67.75) * mm, "end": v(-24.44, 77.75) * mm});
            skLineSegment(sketch, "E53.3.8.2", {"start": v(-24.44, 77.75) * mm, "end": v(-34.44, 77.75) * mm});
            skLineSegment(sketch, "E53.3.8.3", {"start": v(-24.44, 67.75) * mm, "end": v(-34.44, 67.75) * mm});
            skLineSegment(sketch, "E53.3.8.4", {"start": v(-34.44, 67.75) * mm, "end": v(-34.44, 77.75) * mm});
            skPoint(sketch, "E53.4.0.0", {"position": v(-14.44, -75.25) * mm});
            skLineSegment(sketch, "E53.4.0.1", {"start": v(-9.44, -80.25) * mm, "end": v(-9.44, -70.25) * mm});
            skLineSegment(sketch, "E53.4.0.2", {"start": v(-9.44, -70.25) * mm, "end": v(-19.44, -70.25) * mm});
            skLineSegment(sketch, "E53.4.0.3", {"start": v(-9.44, -80.25) * mm, "end": v(-19.44, -80.25) * mm});
            skLineSegment(sketch, "E53.4.0.4", {"start": v(-19.44, -80.25) * mm, "end": v(-19.44, -70.25) * mm});
            skPoint(sketch, "E53.4.1.0", {"position": v(-14.44, -56.75) * mm});
            skLineSegment(sketch, "E53.4.1.1", {"start": v(-9.44, -61.75) * mm, "end": v(-9.44, -51.75) * mm});
            skLineSegment(sketch, "E53.4.1.2", {"start": v(-9.44, -51.75) * mm, "end": v(-19.44, -51.75) * mm});
            skLineSegment(sketch, "E53.4.1.3", {"start": v(-9.44, -61.75) * mm, "end": v(-19.44, -61.75) * mm});
            skLineSegment(sketch, "E53.4.1.4", {"start": v(-19.44, -61.75) * mm, "end": v(-19.44, -51.75) * mm});
            skPoint(sketch, "E53.4.2.0", {"position": v(-14.44, -38.25) * mm});
            skLineSegment(sketch, "E53.4.2.1", {"start": v(-9.44, -43.25) * mm, "end": v(-9.44, -33.25) * mm});
            skLineSegment(sketch, "E53.4.2.2", {"start": v(-9.44, -33.25) * mm, "end": v(-19.44, -33.25) * mm});
            skLineSegment(sketch, "E53.4.2.3", {"start": v(-9.44, -43.25) * mm, "end": v(-19.44, -43.25) * mm});
            skLineSegment(sketch, "E53.4.2.4", {"start": v(-19.44, -43.25) * mm, "end": v(-19.44, -33.25) * mm});
            skPoint(sketch, "E53.4.3.0", {"position": v(-14.44, -19.75) * mm});
            skLineSegment(sketch, "E53.4.3.1", {"start": v(-9.44, -24.75) * mm, "end": v(-9.44, -14.75) * mm});
            skLineSegment(sketch, "E53.4.3.2", {"start": v(-9.44, -14.75) * mm, "end": v(-19.44, -14.75) * mm});
            skLineSegment(sketch, "E53.4.3.3", {"start": v(-9.44, -24.75) * mm, "end": v(-19.44, -24.75) * mm});
            skLineSegment(sketch, "E53.4.3.4", {"start": v(-19.44, -24.75) * mm, "end": v(-19.44, -14.75) * mm});
            skPoint(sketch, "E53.4.5.0", {"position": v(-14.44, 17.25) * mm});
            skLineSegment(sketch, "E53.4.5.1", {"start": v(-9.44, 12.25) * mm, "end": v(-9.44, 22.25) * mm});
            skLineSegment(sketch, "E53.4.5.2", {"start": v(-9.44, 22.25) * mm, "end": v(-19.44, 22.25) * mm});
            skLineSegment(sketch, "E53.4.5.3", {"start": v(-9.44, 12.25) * mm, "end": v(-19.44, 12.25) * mm});
            skLineSegment(sketch, "E53.4.5.4", {"start": v(-19.44, 12.25) * mm, "end": v(-19.44, 22.25) * mm});
            skPoint(sketch, "E53.4.6.0", {"position": v(-14.44, 35.75) * mm});
            skLineSegment(sketch, "E53.4.6.1", {"start": v(-9.44, 30.75) * mm, "end": v(-9.44, 40.75) * mm});
            skLineSegment(sketch, "E53.4.6.2", {"start": v(-9.44, 40.75) * mm, "end": v(-19.44, 40.75) * mm});
            skLineSegment(sketch, "E53.4.6.3", {"start": v(-9.44, 30.75) * mm, "end": v(-19.44, 30.75) * mm});
            skLineSegment(sketch, "E53.4.6.4", {"start": v(-19.44, 30.75) * mm, "end": v(-19.44, 40.75) * mm});
            skPoint(sketch, "E53.4.7.0", {"position": v(-14.44, 54.25) * mm});
            skLineSegment(sketch, "E53.4.7.1", {"start": v(-9.44, 49.25) * mm, "end": v(-9.44, 59.25) * mm});
            skLineSegment(sketch, "E53.4.7.2", {"start": v(-9.44, 59.25) * mm, "end": v(-19.44, 59.25) * mm});
            skLineSegment(sketch, "E53.4.7.3", {"start": v(-9.44, 49.25) * mm, "end": v(-19.44, 49.25) * mm});
            skLineSegment(sketch, "E53.4.7.4", {"start": v(-19.44, 49.25) * mm, "end": v(-19.44, 59.25) * mm});
            skPoint(sketch, "E53.4.8.0", {"position": v(-14.44, 72.75) * mm});
            skLineSegment(sketch, "E53.4.8.1", {"start": v(-9.44, 67.75) * mm, "end": v(-9.44, 77.75) * mm});
            skLineSegment(sketch, "E53.4.8.2", {"start": v(-9.44, 77.75) * mm, "end": v(-19.44, 77.75) * mm});
            skLineSegment(sketch, "E53.4.8.3", {"start": v(-9.44, 67.75) * mm, "end": v(-19.44, 67.75) * mm});
            skLineSegment(sketch, "E53.4.8.4", {"start": v(-19.44, 67.75) * mm, "end": v(-19.44, 77.75) * mm});
            skPoint(sketch, "E53.5.0.0", {"position": v(0.56, -75.25) * mm});
            skLineSegment(sketch, "E53.5.0.1", {"start": v(5.56, -80.25) * mm, "end": v(5.56, -70.25) * mm});
            skLineSegment(sketch, "E53.5.0.2", {"start": v(5.56, -70.25) * mm, "end": v(-4.44, -70.25) * mm});
            skLineSegment(sketch, "E53.5.0.3", {"start": v(5.56, -80.25) * mm, "end": v(-4.44, -80.25) * mm});
            skLineSegment(sketch, "E53.5.0.4", {"start": v(-4.44, -80.25) * mm, "end": v(-4.44, -70.25) * mm});
            skPoint(sketch, "E53.5.1.0", {"position": v(0.56, -56.75) * mm});
            skLineSegment(sketch, "E53.5.1.1", {"start": v(5.56, -61.75) * mm, "end": v(5.56, -51.75) * mm});
            skLineSegment(sketch, "E53.5.1.2", {"start": v(5.56, -51.75) * mm, "end": v(-4.44, -51.75) * mm});
            skLineSegment(sketch, "E53.5.1.3", {"start": v(5.56, -61.75) * mm, "end": v(-4.44, -61.75) * mm});
            skLineSegment(sketch, "E53.5.1.4", {"start": v(-4.44, -61.75) * mm, "end": v(-4.44, -51.75) * mm});
            skPoint(sketch, "E53.5.2.0", {"position": v(0.56, -38.25) * mm});
            skLineSegment(sketch, "E53.5.2.1", {"start": v(5.56, -43.25) * mm, "end": v(5.56, -33.25) * mm});
            skLineSegment(sketch, "E53.5.2.2", {"start": v(5.56, -33.25) * mm, "end": v(-4.44, -33.25) * mm});
            skLineSegment(sketch, "E53.5.2.3", {"start": v(5.56, -43.25) * mm, "end": v(-4.44, -43.25) * mm});
            skLineSegment(sketch, "E53.5.2.4", {"start": v(-4.44, -43.25) * mm, "end": v(-4.44, -33.25) * mm});
            skPoint(sketch, "E53.5.3.0", {"position": v(0.56, -19.75) * mm});
            skLineSegment(sketch, "E53.5.3.1", {"start": v(5.56, -24.75) * mm, "end": v(5.56, -14.75) * mm});
            skLineSegment(sketch, "E53.5.3.2", {"start": v(5.56, -14.75) * mm, "end": v(-4.44, -14.75) * mm});
            skLineSegment(sketch, "E53.5.3.3", {"start": v(5.56, -24.75) * mm, "end": v(-4.44, -24.75) * mm});
            skLineSegment(sketch, "E53.5.3.4", {"start": v(-4.44, -24.75) * mm, "end": v(-4.44, -14.75) * mm});
            skPoint(sketch, "E53.5.5.0", {"position": v(0.56, 17.25) * mm});
            skLineSegment(sketch, "E53.5.5.1", {"start": v(5.56, 12.25) * mm, "end": v(5.56, 22.25) * mm});
            skLineSegment(sketch, "E53.5.5.2", {"start": v(5.56, 22.25) * mm, "end": v(-4.44, 22.25) * mm});
            skLineSegment(sketch, "E53.5.5.3", {"start": v(5.56, 12.25) * mm, "end": v(-4.44, 12.25) * mm});
            skLineSegment(sketch, "E53.5.5.4", {"start": v(-4.44, 12.25) * mm, "end": v(-4.44, 22.25) * mm});
            skPoint(sketch, "E53.5.6.0", {"position": v(0.56, 35.75) * mm});
            skLineSegment(sketch, "E53.5.6.1", {"start": v(5.56, 30.75) * mm, "end": v(5.56, 40.75) * mm});
            skLineSegment(sketch, "E53.5.6.2", {"start": v(5.56, 40.75) * mm, "end": v(-4.44, 40.75) * mm});
            skLineSegment(sketch, "E53.5.6.3", {"start": v(5.56, 30.75) * mm, "end": v(-4.44, 30.75) * mm});
            skLineSegment(sketch, "E53.5.6.4", {"start": v(-4.44, 30.75) * mm, "end": v(-4.44, 40.75) * mm});
            skPoint(sketch, "E53.5.7.0", {"position": v(0.56, 54.25) * mm});
            skLineSegment(sketch, "E53.5.7.1", {"start": v(5.56, 49.25) * mm, "end": v(5.56, 59.25) * mm});
            skLineSegment(sketch, "E53.5.7.2", {"start": v(5.56, 59.25) * mm, "end": v(-4.44, 59.25) * mm});
            skLineSegment(sketch, "E53.5.7.3", {"start": v(5.56, 49.25) * mm, "end": v(-4.44, 49.25) * mm});
            skLineSegment(sketch, "E53.5.7.4", {"start": v(-4.44, 49.25) * mm, "end": v(-4.44, 59.25) * mm});
            skPoint(sketch, "E53.5.8.0", {"position": v(0.56, 72.75) * mm});
            skLineSegment(sketch, "E53.5.8.1", {"start": v(5.56, 67.75) * mm, "end": v(5.56, 77.75) * mm});
            skLineSegment(sketch, "E53.5.8.2", {"start": v(5.56, 77.75) * mm, "end": v(-4.44, 77.75) * mm});
            skLineSegment(sketch, "E53.5.8.3", {"start": v(5.56, 67.75) * mm, "end": v(-4.44, 67.75) * mm});
            skLineSegment(sketch, "E53.5.8.4", {"start": v(-4.44, 67.75) * mm, "end": v(-4.44, 77.75) * mm});
            skPoint(sketch, "E53.6.0.0", {"position": v(15.56, -75.25) * mm});
            skLineSegment(sketch, "E53.6.0.1", {"start": v(20.56, -80.25) * mm, "end": v(20.56, -70.25) * mm});
            skLineSegment(sketch, "E53.6.0.2", {"start": v(20.56, -70.25) * mm, "end": v(10.56, -70.25) * mm});
            skLineSegment(sketch, "E53.6.0.3", {"start": v(20.56, -80.25) * mm, "end": v(10.56, -80.25) * mm});
            skLineSegment(sketch, "E53.6.0.4", {"start": v(10.56, -80.25) * mm, "end": v(10.56, -70.25) * mm});
            skPoint(sketch, "E53.6.1.0", {"position": v(15.56, -56.75) * mm});
            skLineSegment(sketch, "E53.6.1.1", {"start": v(20.56, -61.75) * mm, "end": v(20.56, -51.75) * mm});
            skLineSegment(sketch, "E53.6.1.2", {"start": v(20.56, -51.75) * mm, "end": v(10.56, -51.75) * mm});
            skLineSegment(sketch, "E53.6.1.3", {"start": v(20.56, -61.75) * mm, "end": v(10.56, -61.75) * mm});
            skLineSegment(sketch, "E53.6.1.4", {"start": v(10.56, -61.75) * mm, "end": v(10.56, -51.75) * mm});
            skPoint(sketch, "E53.6.2.0", {"position": v(15.56, -38.25) * mm});
            skLineSegment(sketch, "E53.6.2.1", {"start": v(20.56, -43.25) * mm, "end": v(20.56, -33.25) * mm});
            skLineSegment(sketch, "E53.6.2.2", {"start": v(20.56, -33.25) * mm, "end": v(10.56, -33.25) * mm});
            skLineSegment(sketch, "E53.6.2.3", {"start": v(20.56, -43.25) * mm, "end": v(10.56, -43.25) * mm});
            skLineSegment(sketch, "E53.6.2.4", {"start": v(10.56, -43.25) * mm, "end": v(10.56, -33.25) * mm});
            skPoint(sketch, "E53.6.3.0", {"position": v(15.56, -19.75) * mm});
            skLineSegment(sketch, "E53.6.3.1", {"start": v(20.56, -24.75) * mm, "end": v(20.56, -14.75) * mm});
            skLineSegment(sketch, "E53.6.3.2", {"start": v(20.56, -14.75) * mm, "end": v(10.56, -14.75) * mm});
            skLineSegment(sketch, "E53.6.3.3", {"start": v(20.56, -24.75) * mm, "end": v(10.56, -24.75) * mm});
            skLineSegment(sketch, "E53.6.3.4", {"start": v(10.56, -24.75) * mm, "end": v(10.56, -14.75) * mm});
            skPoint(sketch, "E53.6.5.0", {"position": v(15.56, 17.25) * mm});
            skLineSegment(sketch, "E53.6.5.1", {"start": v(20.56, 12.25) * mm, "end": v(20.56, 22.25) * mm});
            skLineSegment(sketch, "E53.6.5.2", {"start": v(20.56, 22.25) * mm, "end": v(10.56, 22.25) * mm});
            skLineSegment(sketch, "E53.6.5.3", {"start": v(20.56, 12.25) * mm, "end": v(10.56, 12.25) * mm});
            skLineSegment(sketch, "E53.6.5.4", {"start": v(10.56, 12.25) * mm, "end": v(10.56, 22.25) * mm});
            skPoint(sketch, "E53.6.6.0", {"position": v(15.56, 35.75) * mm});
            skLineSegment(sketch, "E53.6.6.1", {"start": v(20.56, 30.75) * mm, "end": v(20.56, 40.75) * mm});
            skLineSegment(sketch, "E53.6.6.2", {"start": v(20.56, 40.75) * mm, "end": v(10.56, 40.75) * mm});
            skLineSegment(sketch, "E53.6.6.3", {"start": v(20.56, 30.75) * mm, "end": v(10.56, 30.75) * mm});
            skLineSegment(sketch, "E53.6.6.4", {"start": v(10.56, 30.75) * mm, "end": v(10.56, 40.75) * mm});
            skPoint(sketch, "E53.6.7.0", {"position": v(15.56, 54.25) * mm});
            skLineSegment(sketch, "E53.6.7.1", {"start": v(20.56, 49.25) * mm, "end": v(20.56, 59.25) * mm});
            skLineSegment(sketch, "E53.6.7.2", {"start": v(20.56, 59.25) * mm, "end": v(10.56, 59.25) * mm});
            skLineSegment(sketch, "E53.6.7.3", {"start": v(20.56, 49.25) * mm, "end": v(10.56, 49.25) * mm});
            skLineSegment(sketch, "E53.6.7.4", {"start": v(10.56, 49.25) * mm, "end": v(10.56, 59.25) * mm});
            skPoint(sketch, "E53.6.8.0", {"position": v(15.56, 72.75) * mm});
            skLineSegment(sketch, "E53.6.8.1", {"start": v(20.56, 67.75) * mm, "end": v(20.56, 77.75) * mm});
            skLineSegment(sketch, "E53.6.8.2", {"start": v(20.56, 77.75) * mm, "end": v(10.56, 77.75) * mm});
            skLineSegment(sketch, "E53.6.8.3", {"start": v(20.56, 67.75) * mm, "end": v(10.56, 67.75) * mm});
            skLineSegment(sketch, "E53.6.8.4", {"start": v(10.56, 67.75) * mm, "end": v(10.56, 77.75) * mm});
            skPoint(sketch, "E53.7.0.0", {"position": v(30.56, -75.25) * mm});
            skLineSegment(sketch, "E53.7.0.1", {"start": v(35.56, -80.25) * mm, "end": v(35.56, -70.25) * mm});
            skLineSegment(sketch, "E53.7.0.2", {"start": v(35.56, -70.25) * mm, "end": v(25.56, -70.25) * mm});
            skLineSegment(sketch, "E53.7.0.3", {"start": v(35.56, -80.25) * mm, "end": v(25.56, -80.25) * mm});
            skLineSegment(sketch, "E53.7.0.4", {"start": v(25.56, -80.25) * mm, "end": v(25.56, -70.25) * mm});
            skPoint(sketch, "E53.7.1.0", {"position": v(30.56, -56.75) * mm});
            skLineSegment(sketch, "E53.7.1.1", {"start": v(35.56, -61.75) * mm, "end": v(35.56, -51.75) * mm});
            skLineSegment(sketch, "E53.7.1.2", {"start": v(35.56, -51.75) * mm, "end": v(25.56, -51.75) * mm});
            skLineSegment(sketch, "E53.7.1.3", {"start": v(35.56, -61.75) * mm, "end": v(25.56, -61.75) * mm});
            skLineSegment(sketch, "E53.7.1.4", {"start": v(25.56, -61.75) * mm, "end": v(25.56, -51.75) * mm});
            skPoint(sketch, "E53.7.2.0", {"position": v(30.56, -38.25) * mm});
            skLineSegment(sketch, "E53.7.2.1", {"start": v(35.56, -43.25) * mm, "end": v(35.56, -33.25) * mm});
            skLineSegment(sketch, "E53.7.2.2", {"start": v(35.56, -33.25) * mm, "end": v(25.56, -33.25) * mm});
            skLineSegment(sketch, "E53.7.2.3", {"start": v(35.56, -43.25) * mm, "end": v(25.56, -43.25) * mm});
            skLineSegment(sketch, "E53.7.2.4", {"start": v(25.56, -43.25) * mm, "end": v(25.56, -33.25) * mm});
            skPoint(sketch, "E53.7.3.0", {"position": v(30.56, -19.75) * mm});
            skLineSegment(sketch, "E53.7.3.1", {"start": v(35.56, -24.75) * mm, "end": v(35.56, -14.75) * mm});
            skLineSegment(sketch, "E53.7.3.2", {"start": v(35.56, -14.75) * mm, "end": v(25.56, -14.75) * mm});
            skLineSegment(sketch, "E53.7.3.3", {"start": v(35.56, -24.75) * mm, "end": v(25.56, -24.75) * mm});
            skLineSegment(sketch, "E53.7.3.4", {"start": v(25.56, -24.75) * mm, "end": v(25.56, -14.75) * mm});
            skPoint(sketch, "E53.7.5.0", {"position": v(30.56, 17.25) * mm});
            skLineSegment(sketch, "E53.7.5.1", {"start": v(35.56, 12.25) * mm, "end": v(35.56, 22.25) * mm});
            skLineSegment(sketch, "E53.7.5.2", {"start": v(35.56, 22.25) * mm, "end": v(25.56, 22.25) * mm});
            skLineSegment(sketch, "E53.7.5.3", {"start": v(35.56, 12.25) * mm, "end": v(25.56, 12.25) * mm});
            skLineSegment(sketch, "E53.7.5.4", {"start": v(25.56, 12.25) * mm, "end": v(25.56, 22.25) * mm});
            skPoint(sketch, "E53.7.6.0", {"position": v(30.56, 35.75) * mm});
            skLineSegment(sketch, "E53.7.6.1", {"start": v(35.56, 30.75) * mm, "end": v(35.56, 40.75) * mm});
            skLineSegment(sketch, "E53.7.6.2", {"start": v(35.56, 40.75) * mm, "end": v(25.56, 40.75) * mm});
            skLineSegment(sketch, "E53.7.6.3", {"start": v(35.56, 30.75) * mm, "end": v(25.56, 30.75) * mm});
            skLineSegment(sketch, "E53.7.6.4", {"start": v(25.56, 30.75) * mm, "end": v(25.56, 40.75) * mm});
            skPoint(sketch, "E53.7.7.0", {"position": v(30.56, 54.25) * mm});
            skLineSegment(sketch, "E53.7.7.1", {"start": v(35.56, 49.25) * mm, "end": v(35.56, 59.25) * mm});
            skLineSegment(sketch, "E53.7.7.2", {"start": v(35.56, 59.25) * mm, "end": v(25.56, 59.25) * mm});
            skLineSegment(sketch, "E53.7.7.3", {"start": v(35.56, 49.25) * mm, "end": v(25.56, 49.25) * mm});
            skLineSegment(sketch, "E53.7.7.4", {"start": v(25.56, 49.25) * mm, "end": v(25.56, 59.25) * mm});
            skPoint(sketch, "E53.7.8.0", {"position": v(30.56, 72.75) * mm});
            skLineSegment(sketch, "E53.7.8.1", {"start": v(35.56, 67.75) * mm, "end": v(35.56, 77.75) * mm});
            skLineSegment(sketch, "E53.7.8.2", {"start": v(35.56, 77.75) * mm, "end": v(25.56, 77.75) * mm});
            skLineSegment(sketch, "E53.7.8.3", {"start": v(35.56, 67.75) * mm, "end": v(25.56, 67.75) * mm});
            skLineSegment(sketch, "E53.7.8.4", {"start": v(25.56, 67.75) * mm, "end": v(25.56, 77.75) * mm});
            skPoint(sketch, "E53.8.0.0", {"position": v(45.56, -75.25) * mm});
            skLineSegment(sketch, "E53.8.0.1", {"start": v(50.56, -80.25) * mm, "end": v(50.56, -70.25) * mm});
            skLineSegment(sketch, "E53.8.0.2", {"start": v(50.56, -70.25) * mm, "end": v(40.56, -70.25) * mm});
            skLineSegment(sketch, "E53.8.0.3", {"start": v(50.56, -80.25) * mm, "end": v(40.56, -80.25) * mm});
            skLineSegment(sketch, "E53.8.0.4", {"start": v(40.56, -80.25) * mm, "end": v(40.56, -70.25) * mm});
            skPoint(sketch, "E53.8.1.0", {"position": v(45.56, -56.75) * mm});
            skLineSegment(sketch, "E53.8.1.1", {"start": v(50.56, -61.75) * mm, "end": v(50.56, -51.75) * mm});
            skLineSegment(sketch, "E53.8.1.2", {"start": v(50.56, -51.75) * mm, "end": v(40.56, -51.75) * mm});
            skLineSegment(sketch, "E53.8.1.3", {"start": v(50.56, -61.75) * mm, "end": v(40.56, -61.75) * mm});
            skLineSegment(sketch, "E53.8.1.4", {"start": v(40.56, -61.75) * mm, "end": v(40.56, -51.75) * mm});
            skPoint(sketch, "E53.8.2.0", {"position": v(45.56, -38.25) * mm});
            skLineSegment(sketch, "E53.8.2.1", {"start": v(50.56, -43.25) * mm, "end": v(50.56, -33.25) * mm});
            skLineSegment(sketch, "E53.8.2.2", {"start": v(50.56, -33.25) * mm, "end": v(40.56, -33.25) * mm});
            skLineSegment(sketch, "E53.8.2.3", {"start": v(50.56, -43.25) * mm, "end": v(40.56, -43.25) * mm});
            skLineSegment(sketch, "E53.8.2.4", {"start": v(40.56, -43.25) * mm, "end": v(40.56, -33.25) * mm});
            skPoint(sketch, "E53.8.3.0", {"position": v(45.56, -19.75) * mm});
            skLineSegment(sketch, "E53.8.3.1", {"start": v(50.56, -24.75) * mm, "end": v(50.56, -14.75) * mm});
            skLineSegment(sketch, "E53.8.3.2", {"start": v(50.56, -14.75) * mm, "end": v(40.56, -14.75) * mm});
            skLineSegment(sketch, "E53.8.3.3", {"start": v(50.56, -24.75) * mm, "end": v(40.56, -24.75) * mm});
            skLineSegment(sketch, "E53.8.3.4", {"start": v(40.56, -24.75) * mm, "end": v(40.56, -14.75) * mm});
            skPoint(sketch, "E53.8.5.0", {"position": v(45.56, 17.25) * mm});
            skLineSegment(sketch, "E53.8.5.1", {"start": v(50.56, 12.25) * mm, "end": v(50.56, 22.25) * mm});
            skLineSegment(sketch, "E53.8.5.2", {"start": v(50.56, 22.25) * mm, "end": v(40.56, 22.25) * mm});
            skLineSegment(sketch, "E53.8.5.3", {"start": v(50.56, 12.25) * mm, "end": v(40.56, 12.25) * mm});
            skLineSegment(sketch, "E53.8.5.4", {"start": v(40.56, 12.25) * mm, "end": v(40.56, 22.25) * mm});
            skPoint(sketch, "E53.8.6.0", {"position": v(45.56, 35.75) * mm});
            skLineSegment(sketch, "E53.8.6.1", {"start": v(50.56, 30.75) * mm, "end": v(50.56, 40.75) * mm});
            skLineSegment(sketch, "E53.8.6.2", {"start": v(50.56, 40.75) * mm, "end": v(40.56, 40.75) * mm});
            skLineSegment(sketch, "E53.8.6.3", {"start": v(50.56, 30.75) * mm, "end": v(40.56, 30.75) * mm});
            skLineSegment(sketch, "E53.8.6.4", {"start": v(40.56, 30.75) * mm, "end": v(40.56, 40.75) * mm});
            skPoint(sketch, "E53.8.7.0", {"position": v(45.56, 54.25) * mm});
            skLineSegment(sketch, "E53.8.7.1", {"start": v(50.56, 49.25) * mm, "end": v(50.56, 59.25) * mm});
            skLineSegment(sketch, "E53.8.7.2", {"start": v(50.56, 59.25) * mm, "end": v(40.56, 59.25) * mm});
            skLineSegment(sketch, "E53.8.7.3", {"start": v(50.56, 49.25) * mm, "end": v(40.56, 49.25) * mm});
            skLineSegment(sketch, "E53.8.7.4", {"start": v(40.56, 49.25) * mm, "end": v(40.56, 59.25) * mm});
            skPoint(sketch, "E53.8.8.0", {"position": v(45.56, 72.75) * mm});
            skLineSegment(sketch, "E53.8.8.1", {"start": v(50.56, 67.75) * mm, "end": v(50.56, 77.75) * mm});
            skLineSegment(sketch, "E53.8.8.2", {"start": v(50.56, 77.75) * mm, "end": v(40.56, 77.75) * mm});
            skLineSegment(sketch, "E53.8.8.3", {"start": v(50.56, 67.75) * mm, "end": v(40.56, 67.75) * mm});
            skLineSegment(sketch, "E53.8.8.4", {"start": v(40.56, 67.75) * mm, "end": v(40.56, 77.75) * mm});
            skPoint(sketch, "E53.9.0.0", {"position": v(60.56, -75.25) * mm});
            skLineSegment(sketch, "E53.9.0.1", {"start": v(65.56, -80.25) * mm, "end": v(65.56, -70.25) * mm});
            skLineSegment(sketch, "E53.9.0.2", {"start": v(65.56, -70.25) * mm, "end": v(55.56, -70.25) * mm});
            skLineSegment(sketch, "E53.9.0.3", {"start": v(65.56, -80.25) * mm, "end": v(55.56, -80.25) * mm});
            skLineSegment(sketch, "E53.9.0.4", {"start": v(55.56, -80.25) * mm, "end": v(55.56, -70.25) * mm});
            skPoint(sketch, "E53.9.1.0", {"position": v(60.56, -56.75) * mm});
            skLineSegment(sketch, "E53.9.1.1", {"start": v(65.56, -61.75) * mm, "end": v(65.56, -51.75) * mm});
            skLineSegment(sketch, "E53.9.1.2", {"start": v(65.56, -51.75) * mm, "end": v(55.56, -51.75) * mm});
            skLineSegment(sketch, "E53.9.1.3", {"start": v(65.56, -61.75) * mm, "end": v(55.56, -61.75) * mm});
            skLineSegment(sketch, "E53.9.1.4", {"start": v(55.56, -61.75) * mm, "end": v(55.56, -51.75) * mm});
            skPoint(sketch, "E53.9.2.0", {"position": v(60.56, -38.25) * mm});
            skLineSegment(sketch, "E53.9.2.1", {"start": v(65.56, -43.25) * mm, "end": v(65.56, -33.25) * mm});
            skLineSegment(sketch, "E53.9.2.2", {"start": v(65.56, -33.25) * mm, "end": v(55.56, -33.25) * mm});
            skLineSegment(sketch, "E53.9.2.3", {"start": v(65.56, -43.25) * mm, "end": v(55.56, -43.25) * mm});
            skLineSegment(sketch, "E53.9.2.4", {"start": v(55.56, -43.25) * mm, "end": v(55.56, -33.25) * mm});
            skPoint(sketch, "E53.9.3.0", {"position": v(60.56, -19.75) * mm});
            skLineSegment(sketch, "E53.9.3.1", {"start": v(65.56, -24.75) * mm, "end": v(65.56, -14.75) * mm});
            skLineSegment(sketch, "E53.9.3.2", {"start": v(65.56, -14.75) * mm, "end": v(55.56, -14.75) * mm});
            skLineSegment(sketch, "E53.9.3.3", {"start": v(65.56, -24.75) * mm, "end": v(55.56, -24.75) * mm});
            skLineSegment(sketch, "E53.9.3.4", {"start": v(55.56, -24.75) * mm, "end": v(55.56, -14.75) * mm});
            skPoint(sketch, "E53.9.5.0", {"position": v(60.56, 17.25) * mm});
            skLineSegment(sketch, "E53.9.5.1", {"start": v(65.56, 12.25) * mm, "end": v(65.56, 22.25) * mm});
            skLineSegment(sketch, "E53.9.5.2", {"start": v(65.56, 22.25) * mm, "end": v(55.56, 22.25) * mm});
            skLineSegment(sketch, "E53.9.5.3", {"start": v(65.56, 12.25) * mm, "end": v(55.56, 12.25) * mm});
            skLineSegment(sketch, "E53.9.5.4", {"start": v(55.56, 12.25) * mm, "end": v(55.56, 22.25) * mm});
            skPoint(sketch, "E53.9.6.0", {"position": v(60.56, 35.75) * mm});
            skLineSegment(sketch, "E53.9.6.1", {"start": v(65.56, 30.75) * mm, "end": v(65.56, 40.75) * mm});
            skLineSegment(sketch, "E53.9.6.2", {"start": v(65.56, 40.75) * mm, "end": v(55.56, 40.75) * mm});
            skLineSegment(sketch, "E53.9.6.3", {"start": v(65.56, 30.75) * mm, "end": v(55.56, 30.75) * mm});
            skLineSegment(sketch, "E53.9.6.4", {"start": v(55.56, 30.75) * mm, "end": v(55.56, 40.75) * mm});
            skPoint(sketch, "E53.9.7.0", {"position": v(60.56, 54.25) * mm});
            skLineSegment(sketch, "E53.9.7.1", {"start": v(65.56, 49.25) * mm, "end": v(65.56, 59.25) * mm});
            skLineSegment(sketch, "E53.9.7.2", {"start": v(65.56, 59.25) * mm, "end": v(55.56, 59.25) * mm});
            skLineSegment(sketch, "E53.9.7.3", {"start": v(65.56, 49.25) * mm, "end": v(55.56, 49.25) * mm});
            skLineSegment(sketch, "E53.9.7.4", {"start": v(55.56, 49.25) * mm, "end": v(55.56, 59.25) * mm});
            skPoint(sketch, "E53.9.8.0", {"position": v(60.56, 72.75) * mm});
            skLineSegment(sketch, "E53.9.8.1", {"start": v(65.56, 67.75) * mm, "end": v(65.56, 77.75) * mm});
            skLineSegment(sketch, "E53.9.8.2", {"start": v(65.56, 77.75) * mm, "end": v(55.56, 77.75) * mm});
            skLineSegment(sketch, "E53.9.8.3", {"start": v(65.56, 67.75) * mm, "end": v(55.56, 67.75) * mm});
            skLineSegment(sketch, "E53.9.8.4", {"start": v(55.56, 67.75) * mm, "end": v(55.56, 77.75) * mm});
            skPoint(sketch, "E53.10.0.0", {"position": v(75.56, -75.25) * mm});
            skLineSegment(sketch, "E53.10.0.1", {"start": v(80.56, -80.25) * mm, "end": v(80.56, -70.25) * mm});
            skLineSegment(sketch, "E53.10.0.2", {"start": v(80.56, -70.25) * mm, "end": v(70.56, -70.25) * mm});
            skLineSegment(sketch, "E53.10.0.3", {"start": v(80.56, -80.25) * mm, "end": v(70.56, -80.25) * mm});
            skLineSegment(sketch, "E53.10.0.4", {"start": v(70.56, -80.25) * mm, "end": v(70.56, -70.25) * mm});
            skPoint(sketch, "E53.10.1.0", {"position": v(75.56, -56.75) * mm});
            skLineSegment(sketch, "E53.10.1.1", {"start": v(80.56, -61.75) * mm, "end": v(80.56, -51.75) * mm});
            skLineSegment(sketch, "E53.10.1.2", {"start": v(80.56, -51.75) * mm, "end": v(70.56, -51.75) * mm});
            skLineSegment(sketch, "E53.10.1.3", {"start": v(80.56, -61.75) * mm, "end": v(70.56, -61.75) * mm});
            skLineSegment(sketch, "E53.10.1.4", {"start": v(70.56, -61.75) * mm, "end": v(70.56, -51.75) * mm});
            skPoint(sketch, "E53.10.2.0", {"position": v(75.56, -38.25) * mm});
            skLineSegment(sketch, "E53.10.2.1", {"start": v(80.56, -43.25) * mm, "end": v(80.56, -33.25) * mm});
            skLineSegment(sketch, "E53.10.2.2", {"start": v(80.56, -33.25) * mm, "end": v(70.56, -33.25) * mm});
            skLineSegment(sketch, "E53.10.2.3", {"start": v(80.56, -43.25) * mm, "end": v(70.56, -43.25) * mm});
            skLineSegment(sketch, "E53.10.2.4", {"start": v(70.56, -43.25) * mm, "end": v(70.56, -33.25) * mm});
            skPoint(sketch, "E53.10.3.0", {"position": v(75.56, -19.75) * mm});
            skLineSegment(sketch, "E53.10.3.1", {"start": v(80.56, -24.75) * mm, "end": v(80.56, -14.75) * mm});
            skLineSegment(sketch, "E53.10.3.2", {"start": v(80.56, -14.75) * mm, "end": v(70.56, -14.75) * mm});
            skLineSegment(sketch, "E53.10.3.3", {"start": v(80.56, -24.75) * mm, "end": v(70.56, -24.75) * mm});
            skLineSegment(sketch, "E53.10.3.4", {"start": v(70.56, -24.75) * mm, "end": v(70.56, -14.75) * mm});
            skPoint(sketch, "E53.10.5.0", {"position": v(75.56, 17.25) * mm});
            skLineSegment(sketch, "E53.10.5.1", {"start": v(80.56, 12.25) * mm, "end": v(80.56, 22.25) * mm});
            skLineSegment(sketch, "E53.10.5.2", {"start": v(80.56, 22.25) * mm, "end": v(70.56, 22.25) * mm});
            skLineSegment(sketch, "E53.10.5.3", {"start": v(80.56, 12.25) * mm, "end": v(70.56, 12.25) * mm});
            skLineSegment(sketch, "E53.10.5.4", {"start": v(70.56, 12.25) * mm, "end": v(70.56, 22.25) * mm});
            skPoint(sketch, "E53.10.6.0", {"position": v(75.56, 35.75) * mm});
            skLineSegment(sketch, "E53.10.6.1", {"start": v(80.56, 30.75) * mm, "end": v(80.56, 40.75) * mm});
            skLineSegment(sketch, "E53.10.6.2", {"start": v(80.56, 40.75) * mm, "end": v(70.56, 40.75) * mm});
            skLineSegment(sketch, "E53.10.6.3", {"start": v(80.56, 30.75) * mm, "end": v(70.56, 30.75) * mm});
            skLineSegment(sketch, "E53.10.6.4", {"start": v(70.56, 30.75) * mm, "end": v(70.56, 40.75) * mm});
            skPoint(sketch, "E53.10.7.0", {"position": v(75.56, 54.25) * mm});
            skLineSegment(sketch, "E53.10.7.1", {"start": v(80.56, 49.25) * mm, "end": v(80.56, 59.25) * mm});
            skLineSegment(sketch, "E53.10.7.2", {"start": v(80.56, 59.25) * mm, "end": v(70.56, 59.25) * mm});
            skLineSegment(sketch, "E53.10.7.3", {"start": v(80.56, 49.25) * mm, "end": v(70.56, 49.25) * mm});
            skLineSegment(sketch, "E53.10.7.4", {"start": v(70.56, 49.25) * mm, "end": v(70.56, 59.25) * mm});
            skPoint(sketch, "E53.10.8.0", {"position": v(75.56, 72.75) * mm});
            skLineSegment(sketch, "E53.10.8.1", {"start": v(80.56, 67.75) * mm, "end": v(80.56, 77.75) * mm});
            skLineSegment(sketch, "E53.10.8.2", {"start": v(80.56, 77.75) * mm, "end": v(70.56, 77.75) * mm});
            skLineSegment(sketch, "E53.10.8.3", {"start": v(80.56, 67.75) * mm, "end": v(70.56, 67.75) * mm});
            skLineSegment(sketch, "E53.10.8.4", {"start": v(70.56, 67.75) * mm, "end": v(70.56, 77.75) * mm});
            skLineSegment(sketch, "E53.direction1", {"start": v(-79.44, -80.25) * mm, "end": v(-64.44, -80.25) * mm, "construction": true});
            skLineSegment(sketch, "E53.direction2", {"start": v(-79.44, -80.25) * mm, "end": v(-79.44, -61.75) * mm, "construction": true});
            skSolve(sketch);
        }
        {
            var Q0;
            Q0 = qSketchRegion(id + "F24", true);
            extrude(context, id + "F25", {"entities" : qUnion([Q0]), "operationType" : NewBodyOperationType.REMOVE, "endBound" : BoundingType.SYMMETRIC, "oppositeDirection" : true, "depth" : 300 * mm, "offsetDistance" : 25 * mm});
        }
        {
            var Q0;
            Q0=makeQuery(id+"F2.imprint","IMPRINT",FACE,{"disambiguationData":[TD([[makeQuery(id+"F2.imprint","IMPRINT",EDGE,{"derivedFrom":sQuery(id+"F2.wireOp",EDGE,"E1.bottom")}),-1.0]])]});
            var sketch = newSketch(context, id + "F26", { "sketchPlane" : qUnion([Q0])});
            skLineSegment(sketch, "E54", {"start": v(-117.68, 0) * mm, "end": v(121.84, 0) * mm, "construction": true});
            skLineSegment(sketch, "E55.bottom", {"start": v(-107.47, -2) * mm, "end": v(-112.47, -2) * mm, "construction": true});
            skLineSegment(sketch, "E55.top", {"start": v(-107.47, 2) * mm, "end": v(-112.47, 2) * mm, "construction": true});
            skLineSegment(sketch, "E55.left", {"start": v(-107.47, -2) * mm, "end": v(-107.47, 2) * mm, "construction": true});
            skLineSegment(sketch, "E55.right", {"start": v(-112.47, -2) * mm, "end": v(-112.47, 2) * mm, "construction": true});
            skPoint(sketch, "E55.middle", {"position": v(-109.97, 0) * mm});
            skLineSegment(sketch, "E56.bottom", {"start": v(112.53, -2) * mm, "end": v(107.53, -2) * mm});
            skLineSegment(sketch, "E56.top", {"start": v(112.53, 2) * mm, "end": v(107.53, 2) * mm});
            skLineSegment(sketch, "E56.left", {"start": v(112.53, -2) * mm, "end": v(112.53, 2) * mm});
            skLineSegment(sketch, "E56.right", {"start": v(107.53, -2) * mm, "end": v(107.53, 2) * mm});
            skPoint(sketch, "E56.middle", {"position": v(110.03, 0) * mm});
            skSolve(sketch);
        }
        {
            var Q0;
            Q0 = qSketchRegion(id + "F26", true);
            extrude(context, id + "F27", {"entities" : qUnion([Q0]), "operationType" : NewBodyOperationType.ADD, "oppositeDirection" : true, "depth" : 10 * mm, "offsetDistance" : 25 * mm});
        }
        {
            var Q0;
            Q0=makeQuery(id+"F2.imprint","IMPRINT",FACE,{"disambiguationData":[TD([[makeQuery(id+"F2.imprint","IMPRINT",EDGE,{"derivedFrom":sQuery(id+"F2.wireOp",EDGE,"E1.bottom")}),1.0]])]});
            var sketch = newSketch(context, id + "F28", { "sketchPlane" : qUnion([Q0])});
            skCircle(sketch, "E57", {"center": v(110.08, 0) * mm, "radius": 1.45 * mm});
            skSolve(sketch);
        }
        {
            var Q0;
            Q0 = qSketchRegion(id + "F28", true);
            extrude(context, id + "F29", {"entities" : qUnion([Q0]), "operationType" : NewBodyOperationType.REMOVE, "oppositeDirection" : true, "depth" : 10 * mm, "offsetDistance" : 25 * mm});
        }
        {
            var Q0;
            Q0=makeQuery(id+"F2.imprint","IMPRINT",FACE,{"disambiguationData":[TD([[makeQuery(id+"F2.imprint","IMPRINT",EDGE,{"derivedFrom":sQuery(id+"F2.wireOp",EDGE,"E1.bottom")}),1.0]])]});
            var sketch = newSketch(context, id + "F30", { "sketchPlane" : qUnion([Q0])});
            skLineSegment(sketch, "E58.bottom", {"start": v(-107.3, -2.53) * mm, "end": v(-112.48, -2.53) * mm});
            skLineSegment(sketch, "E58.top", {"start": v(-107.3, 2.53) * mm, "end": v(-112.48, 2.53) * mm});
            skLineSegment(sketch, "E58.left", {"start": v(-107.3, -2.53) * mm, "end": v(-107.3, 2.53) * mm});
            skLineSegment(sketch, "E58.right", {"start": v(-112.48, -2.53) * mm, "end": v(-112.48, 2.53) * mm});
            skPoint(sketch, "E58.middle", {"position": v(-109.89, 0) * mm});
            skSolve(sketch);
        }
        {
            var Q0;
            Q0 = qSketchRegion(id + "F30", true);
            extrude(context, id + "F31", {"entities" : qUnion([Q0]), "operationType" : NewBodyOperationType.ADD, "oppositeDirection" : true, "depth" : 10 * mm, "offsetDistance" : 25 * mm});
        }
        {
            var Q0;
            {var subQ0=sQuery(id+"F30.wireOp",EDGE,"E58.left");Q0=makeQuery(id+"F30.imprint","IMPRINT",FACE,{"disambiguationData":[TD([[makeQuery(id+"F30.imprint","IMPRINT",EDGE,{"derivedFrom":subQ0}),1.0]])]});}
            var sketch = newSketch(context, id + "F32", { "sketchPlane" : qUnion([Q0])});
            skCircle(sketch, "E59", {"center": v(-109.88, 0) * mm, "radius": 1.45 * mm});
            skSolve(sketch);
        }
        {
            var Q0;
            Q0 = qSketchRegion(id + "F32", true);
            extrude(context, id + "F33", {"entities" : qUnion([Q0]), "operationType" : NewBodyOperationType.REMOVE, "oppositeDirection" : true, "depth" : 10 * mm, "offsetDistance" : 25 * mm});
        }
    });
